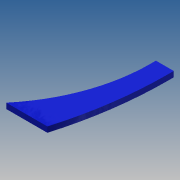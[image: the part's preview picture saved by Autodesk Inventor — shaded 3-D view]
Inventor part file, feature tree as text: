
AUTODESK INVENTOR PART (.ipt)
format: ipt  version: 2015 (Build 190159000, 159)  size: 102,912 bytes
history: native  units: mm
features: extrude x1, sketch x1
ambient origin geometry x8: Origin, YZ Plane, XZ Plane, XY Plane, X Axis, Y Axis, Z Axis, Center Point
bodies: Body1 (feature_tree)
feature tree (2):
  extrude  "Extrusion6"  Depth=40.0mm
  sketch  "Skizze3"  dims[d4=1000.0mm d5=1000.0mm d6=100.0mm d7=550.0mm d8=180.0mm d9=100.0mm d10=100.0mm d11=320.0mm d12=300.0mm d13=350.0mm d14=230.0mm d15=60.0mm d16=-60.0mm d17=130.0mm d18=190.0mm d19=50.0mm d21=283.537414mm d22=40.0mm d23=140.0mm d24=899.502025mm d25=919.104612mm d26=330.793649mm d35=40.0mm d36=0.0mm]
